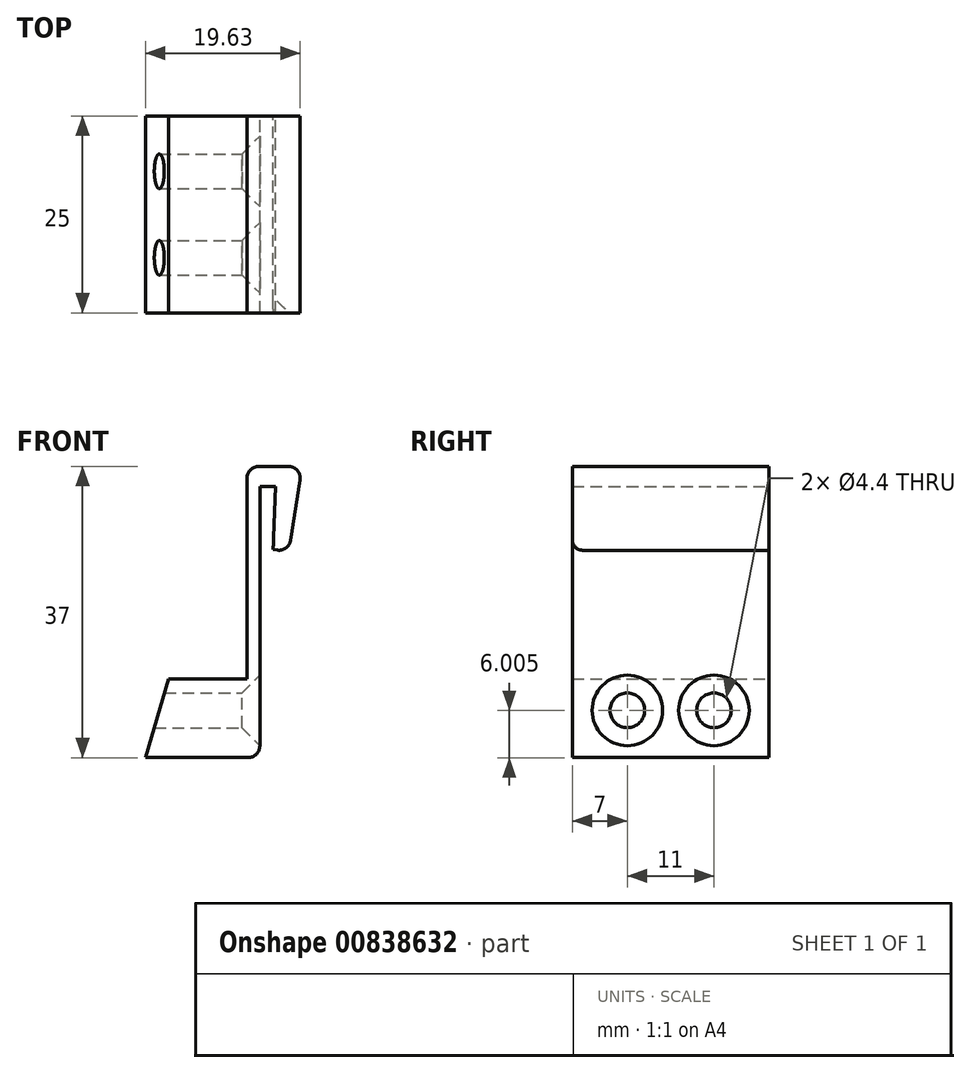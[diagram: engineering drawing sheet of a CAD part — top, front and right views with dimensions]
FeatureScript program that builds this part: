
annotation { "Feature Type Name" : "Feature", "Feature Type Description" : "" }
export const myFeature = defineFeature(function(context is Context, id is Id, definition is map)
    precondition{}
    {
        {
            var Q0;
            Q0=qCreatedBy(makeId("Front.planeOp"),FACE);
            var sketch = newSketch(context, id + "F0", { "sketchPlane" : qUnion([Q0])});
            skLineSegment(sketch, "E0", {"start": v(0, -13.04) * mm, "end": v(0, 14.34) * mm});
            skLineSegment(sketch, "E1", {"start": v(0, 14.34) * mm, "end": v(2, 14.34) * mm});
            skLineSegment(sketch, "E2", {"start": v(2, 14.34) * mm, "end": v(1.7, 6.34) * mm});
            skLineSegment(sketch, "E3", {"start": v(1.7, 6.34) * mm, "end": v(3.68, 6.03) * mm});
            skLineSegment(sketch, "E4", {"start": v(3.68, 6.03) * mm, "end": v(5.38, 16.9) * mm});
            skLineSegment(sketch, "E5", {"start": v(5.38, 16.9) * mm, "end": v(-1.62, 16.9) * mm});
            skLineSegment(sketch, "E6", {"start": v(-1.62, 16.9) * mm, "end": v(-1.62, -10.1) * mm});
            skLineSegment(sketch, "E7", {"start": v(-1.62, -10.1) * mm, "end": v(-11.62, -10.1) * mm});
            skLineSegment(sketch, "E8", {"start": v(-14.5, -20.1) * mm, "end": v(0, -20.1) * mm});
            skLineSegment(sketch, "E9", {"start": v(0, -20.1) * mm, "end": v(0, -13.04) * mm});
            skLineSegment(sketch, "E10", {"start": v(-11.62, -10.1) * mm, "end": v(-14.5, -20.1) * mm});
            skSolve(sketch);
        }
        {
            var Q0;
            Q0=makeQuery(id+"F0.imprint","IMPRINT",FACE,{"disambiguationData":[TD([[makeQuery(id+"F0.imprint","IMPRINT",EDGE,{"derivedFrom":sQuery(id+"F0.wireOp",EDGE,"E0")}),1.0]])]});
            extrude(context, id + "F1", {"entities" : qUnion([Q0]), "depth" : 25 * mm, "offsetDistance" : 25 * mm});
        }
        {
            var Q0;
            Q0=makeQuery(id+"F1.opExtrude","SWEPT_EDGE",EDGE,{"disambiguationData":[OSD([sQuery(id+"F0.wireOp",EDGE,"E5"),sQuery(id+"F0.wireOp",EDGE,"E6")])]});
            var Q1;
            Q1=makeQuery(id+"F1.opExtrude","SWEPT_EDGE",EDGE,{"disambiguationData":[OSD([sQuery(id+"F0.wireOp",EDGE,"E4"),sQuery(id+"F0.wireOp",EDGE,"E5")])]});
            var Q2;
            Q2=makeQuery(id+"F1.opExtrude","SWEPT_EDGE",EDGE,{"disambiguationData":[OSD([sQuery(id+"F0.wireOp",EDGE,"E8"),sQuery(id+"F0.wireOp",EDGE,"E9")])]});
            var Q3;
            Q3=makeQuery(id+"F1.opExtrude","CAP_EDGE",EDGE,{"disambiguationData":[OSD([sQuery(id+"F0.wireOp",EDGE,"E3")])],"isStart":false});
            var Q4;
            Q4=makeQuery(id+"F1.opExtrude","SWEPT_EDGE",EDGE,{"disambiguationData":[OSD([sQuery(id+"F0.wireOp",EDGE,"E3"),sQuery(id+"F0.wireOp",EDGE,"E4")])]});
            fillet(context, id + "F2", {"entities" : qUnion([Q0, Q1, Q2, Q3, Q4]), "radius" : 1.5 * mm, "tangentPropagation" : true, "allowEdgeOverflow" : false});
        }
        {
            var Q0;
            Q0=makeQuery(id+"F1.opExtrude","SWEPT_FACE",FACE,{"disambiguationData":[OSD([sQuery(id+"F0.wireOp",EDGE,"E0"),sQuery(id+"F0.wireOp",EDGE,"E9")])]});
            var sketch = newSketch(context, id + "F3", { "sketchPlane" : qUnion([Q0])});
            skLineSegment(sketch, "E11", {"start": v(-30.22, -14.1) * mm, "end": v(6.5, -14.1) * mm, "construction": true});
            skLineSegment(sketch, "E12", {"start": v(-7, -21.72) * mm, "end": v(-7, -14.86) * mm, "construction": true});
            skLineSegment(sketch, "E13", {"start": v(-18, -21.95) * mm, "end": v(-18, -13.2) * mm, "construction": true});
            skPoint(sketch, "E14", {"position": v(-7, -14.1) * mm});
            skPoint(sketch, "E15", {"position": v(-18, -14.1) * mm});
            skSolve(sketch);
        }
        {
            var Q0;
            Q0=sQuery(id+"F3.wireOp",VERTEX,"E14");
            var Q1;
            Q1=sQuery(id+"F3.wireOp",VERTEX,"E15");
            var Q2;
            Q2=makeQuery(id+"F1.opExtrude","SWEPT_BODY",BODY,{"disambiguationData":[OSD([sQuery(id+"F0.wireOp",EDGE,"E0"),sQuery(id+"F0.wireOp",EDGE,"E1"),sQuery(id+"F0.wireOp",EDGE,"E2"),sQuery(id+"F0.wireOp",EDGE,"E3"),sQuery(id+"F0.wireOp",EDGE,"E4"),sQuery(id+"F0.wireOp",EDGE,"E5"),sQuery(id+"F0.wireOp",EDGE,"E6"),sQuery(id+"F0.wireOp",EDGE,"E7"),sQuery(id+"F0.wireOp",EDGE,"e7G39Qsn-I85n-nhrz-3x4b-e7uau5TgN49u"),sQuery(id+"F0.wireOp",EDGE,"E8"),sQuery(id+"F0.wireOp",EDGE,"E9")])]});
            hole(context, id + "F4", {"style" : HoleStyle.C_SINK, "endStyle" : HoleEndStyle.THROUGH, "standardTappedOrClearance" : lookupTablePath({ "fit" : "Normal", "standard" : "ISO", "size" : "M4", "type" : "Clearance" }), "standardBlindInLast" : lookupTablePath({ "fit" : "Standard", "standard" : "ISO", "size" : "M4", "type" : "Clearance" }), "holeDiameter" : 4.4 * mm, "cSinkDiameter" : 8.96 * mm, "cSinkAngle" : 90 * degree, "majorDiameter" : 5 * mm, "isTappedThrough" : true, "tappedDepth" : 12 * mm, "tapClearance" : 3, "locations" : qUnion([Q0, Q1]), "scope" : qUnion([Q2])});
        }
    });
